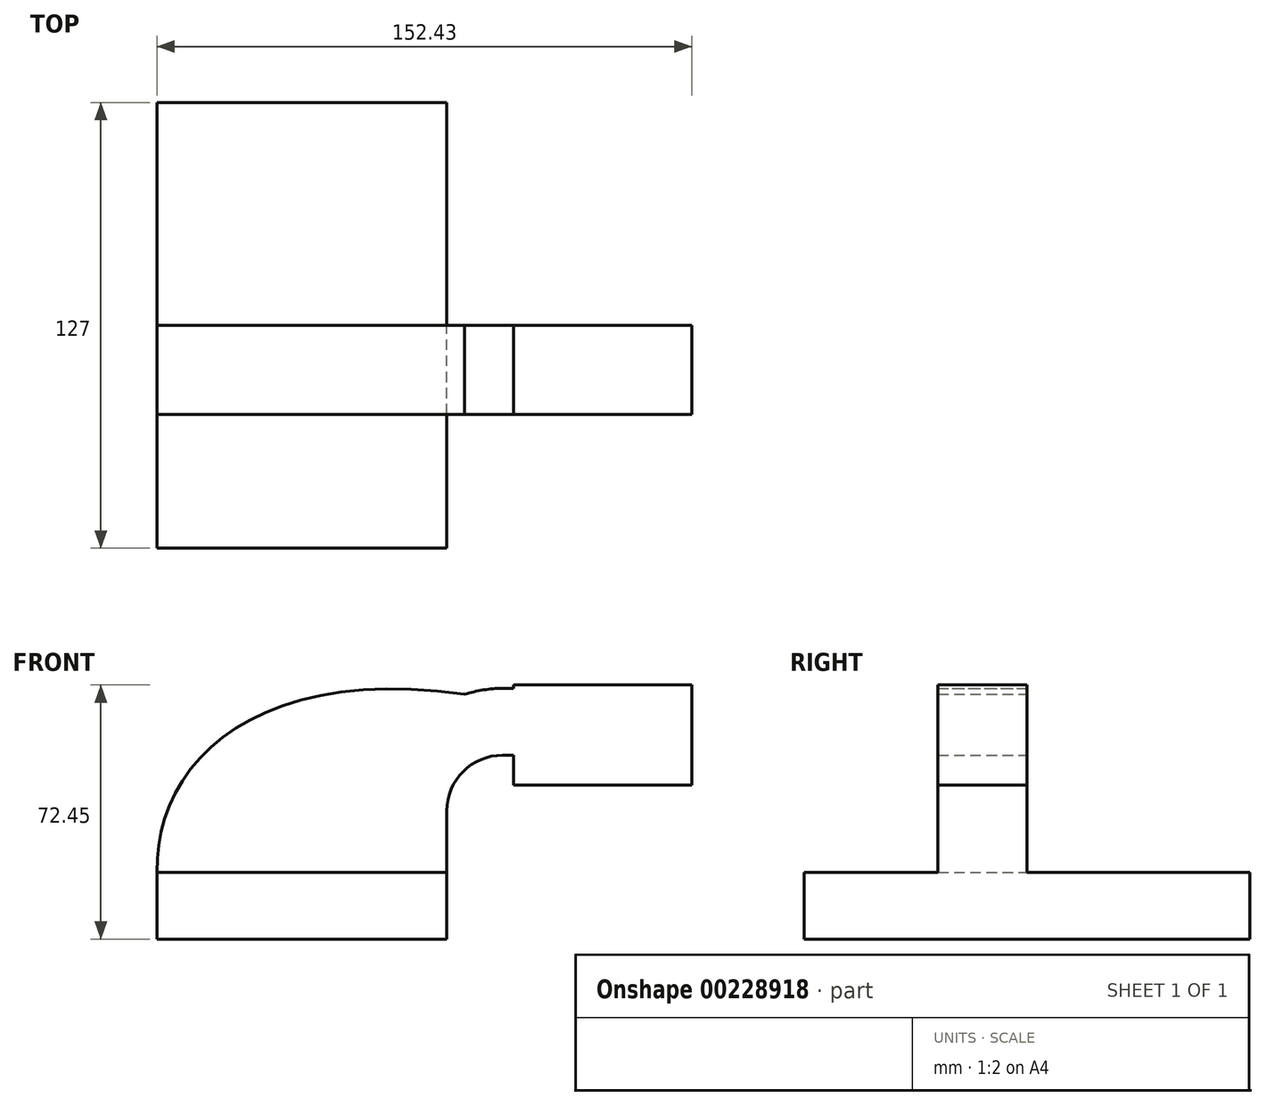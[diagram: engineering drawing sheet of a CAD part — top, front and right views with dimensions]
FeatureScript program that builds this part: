
annotation { "Feature Type Name" : "Feature", "Feature Type Description" : "" }
export const myFeature = defineFeature(function(context is Context, id is Id, definition is map)
    precondition{}
    {
        {
            var Q0;
            Q0=qCreatedBy(makeId("Front.planeOp"),FACE);
            var sketch = newSketch(context, id + "F0", { "sketchPlane" : qUnion([Q0])});
            skLineSegment(sketch, "E0.bottom", {"start": v(-41.28, -9.53) * mm, "end": v(41.28, -9.53) * mm});
            skLineSegment(sketch, "E0.top", {"start": v(-41.28, 9.53) * mm, "end": v(41.28, 9.53) * mm});
            skLineSegment(sketch, "E0.left", {"start": v(-41.28, -9.53) * mm, "end": v(-41.28, 9.53) * mm});
            skLineSegment(sketch, "E0.right", {"start": v(41.28, -9.53) * mm, "end": v(41.28, 9.53) * mm});
            skPoint(sketch, "E0.middle", {"position": v(0, 0) * mm});
            skLineSegment(sketch, "E1.bottom", {"start": v(111.12, 34.34) * mm, "end": v(60.32, 34.34) * mm});
            skLineSegment(sketch, "E1.top", {"start": v(111.12, 62.92) * mm, "end": v(60.32, 62.92) * mm});
            skLineSegment(sketch, "E1.left", {"start": v(111.12, 34.34) * mm, "end": v(111.12, 62.92) * mm});
            skLineSegment(sketch, "E1.right", {"start": v(60.32, 34.34) * mm, "end": v(60.32, 62.92) * mm});
            skPoint(sketch, "E1.middle", {"position": v(85.72, 48.63) * mm});
            skLineSegment(sketch, "E2", {"start": v(41.27, 9.53) * mm, "end": v(41.27, 27) * mm});
            skArc(sketch, "E3", {"start": v(41.27, 27) * mm, "mid": v(45.92, 38.23) * mm, "end": v(57.15, 42.88) * mm});
            skLineSegment(sketch, "E4", {"start": v(57.15, 42.88) * mm, "end": v(109.55, 42.88) * mm});
            skLineSegment(sketch, "E5.0", {"start": v(60.32, 23.83) * mm, "end": v(109.55, 23.83) * mm});
            skLineSegment(sketch, "E5.1", {"start": v(60.32, 9.53) * mm, "end": v(60.32, 23.83) * mm});
            skLineSegment(sketch, "E6.0", {"start": v(57.15, 61.93) * mm, "end": v(109.55, 61.93) * mm});
            skArc(sketch, "E6.1", {"start": v(22.22, 27) * mm, "mid": v(32.45, 51.7) * mm, "end": v(57.15, 61.93) * mm});
            skLineSegment(sketch, "E6.2", {"start": v(22.22, 9.53) * mm, "end": v(22.22, 27) * mm});
            skLineSegment(sketch, "E7", {"start": v(92.67, 34.34) * mm, "end": v(92.67, 61.93) * mm});
            skFitSpline(sketch, "E8", {"points": [v(-41.28, 9.52) * mm, v(46.35, 60.21) * mm], "startDerivative": vector(-2.73, 89.03) * mm, "endDerivative": vector(183.78, -26.22) * mm});
            skSolve(sketch);
        }
        {
            var Q0;
            Q0=makeQuery(id+"F0.imprint","IMPRINT",FACE,{"disambiguationData":[TD([[makeQuery(id+"F0.imprint","IMPRINT",EDGE,{"derivedFrom":sQuery(id+"F0.wireOp",EDGE,"E0.bottom")}),1.0]])]});
            extrude(context, id + "F1", {"entities" : qUnion([Q0]), "endBound" : BoundingType.SYMMETRIC, "depth" : 127 * mm});
        }
        {
            var Q0;
            Q0 = qSketchRegion(id + "F0", true);
            extrude(context, id + "F2", {"entities" : qUnion([Q0]), "operationType" : NewBodyOperationType.ADD, "depth" : 25.4 * mm});
        }
    });
